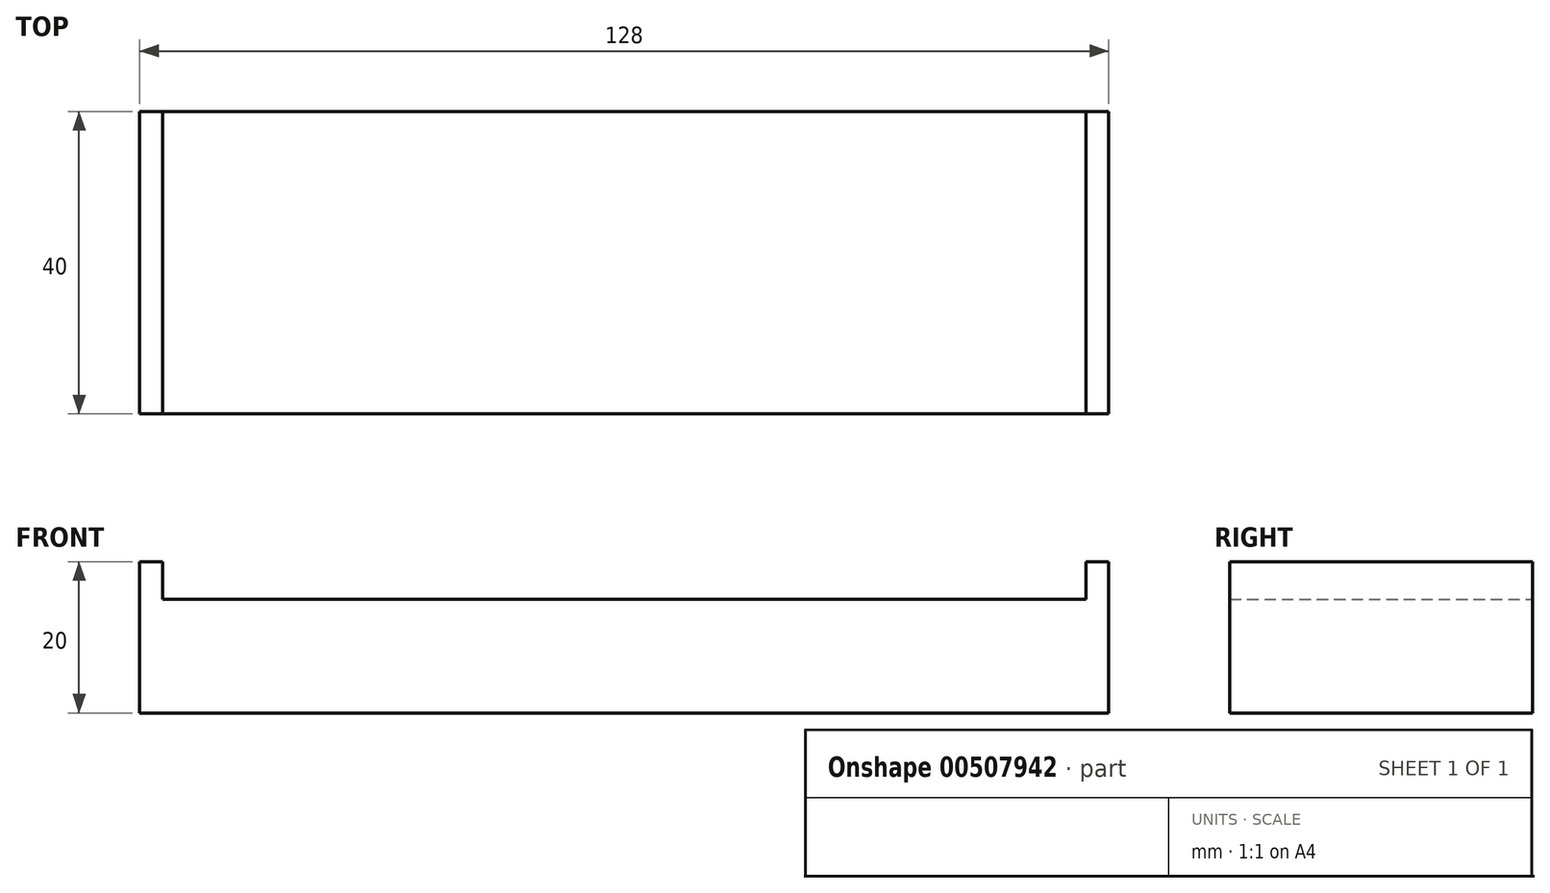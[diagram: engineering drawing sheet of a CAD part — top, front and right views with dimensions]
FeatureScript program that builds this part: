
annotation { "Feature Type Name" : "Feature", "Feature Type Description" : "" }
export const myFeature = defineFeature(function(context is Context, id is Id, definition is map)
    precondition{}
    {
        {
            var Q0;
            Q0=qCreatedBy(makeId("Front.planeOp"),FACE);
            var sketch = newSketch(context, id + "F0", { "sketchPlane" : qUnion([Q0])});
            skLineSegment(sketch, "E0", {"start": v(-109.22, 10.07) * mm, "end": v(-109.22, -9.93) * mm});
            skLineSegment(sketch, "E1", {"start": v(-109.22, -9.93) * mm, "end": v(18.78, -9.93) * mm});
            skLineSegment(sketch, "E2", {"start": v(18.78, -9.93) * mm, "end": v(18.78, 10.07) * mm});
            skLineSegment(sketch, "E3", {"start": v(-106.22, 5.07) * mm, "end": v(-106.22, 10.07) * mm});
            skLineSegment(sketch, "E4", {"start": v(-106.22, 10.07) * mm, "end": v(-109.22, 10.07) * mm});
            skLineSegment(sketch, "E5", {"start": v(18.78, 10.07) * mm, "end": v(15.78, 10.07) * mm});
            skLineSegment(sketch, "E6", {"start": v(15.78, 10.07) * mm, "end": v(15.78, 5.07) * mm});
            skLineSegment(sketch, "E7", {"start": v(15.78, 5.07) * mm, "end": v(-106.22, 5.07) * mm});
            skSolve(sketch);
        }
        {
            var Q0;
            Q0=makeQuery(id+"F0.imprint","IMPRINT",FACE,{"disambiguationData":[TD([[makeQuery(id+"F0.imprint","IMPRINT",EDGE,{"derivedFrom":sQuery(id+"F0.wireOp",EDGE,"E0")}),1.0]])]});
            var Q1;
            Q1=sQuery(id+"F0.wireOp",EDGE,"E1");
            var Q2;
            Q2=sQuery(id+"F0.wireOp",EDGE,"E2");
            var Q3;
            Q3=sQuery(id+"F0.wireOp",EDGE,"E0");
            var Q4;
            Q4=sQuery(id+"F0.wireOp",EDGE,"E6");
            var Q5;
            Q5=sQuery(id+"F0.wireOp",EDGE,"E7");
            var Q6;
            Q6=sQuery(id+"F0.wireOp",EDGE,"E3");
            var Q7;
            Q7=sQuery(id+"F0.wireOp",EDGE,"E5");
            var Q8;
            Q8=sQuery(id+"F0.wireOp",EDGE,"E4");
            extrude(context, id + "F1", {"entities" : qUnion([Q0]), "surfaceEntities" : qUnion([Q1, Q2, Q3, Q4, Q5, Q6, Q7, Q8]), "depth" : 40 * mm});
        }
    });
